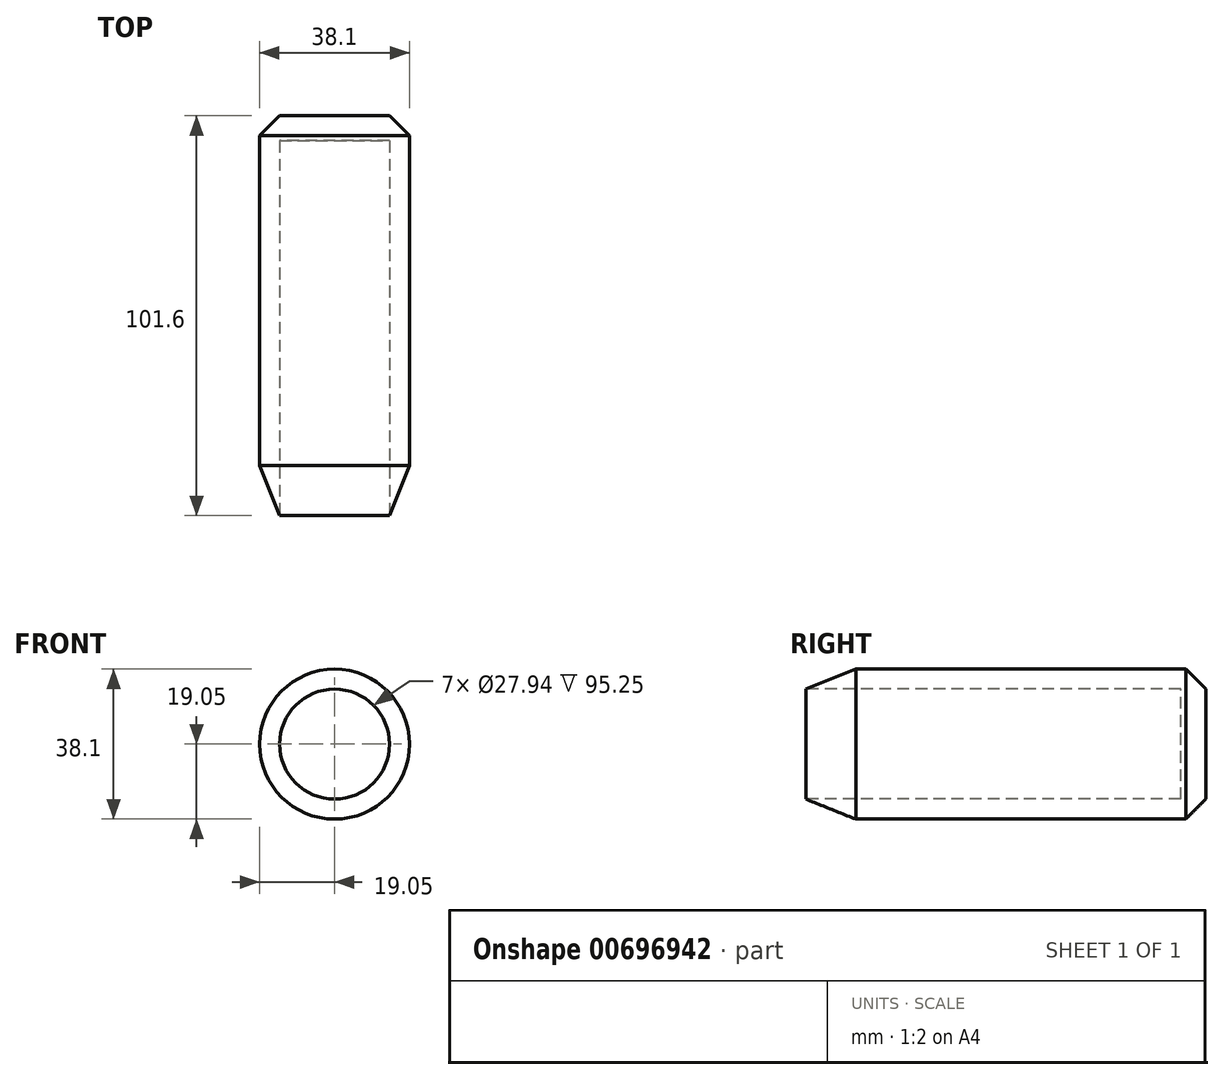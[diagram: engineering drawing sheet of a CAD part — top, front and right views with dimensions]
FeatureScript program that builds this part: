
annotation { "Feature Type Name" : "Feature", "Feature Type Description" : "" }
export const myFeature = defineFeature(function(context is Context, id is Id, definition is map)
    precondition{}
    {
        {
            var Q0;
            Q0=qCreatedBy(makeId("Front.planeOp"),FACE);
            var sketch = newSketch(context, id + "F0", { "sketchPlane" : qUnion([Q0])});
            skCircle(sketch, "E0", {"center": v(0, 0) * mm, "radius": 12.7 * mm});
            skCircle(sketch, "E1", {"center": v(0, 0) * mm, "radius": 19.05 * mm});
            skSolve(sketch);
        }
        {
            var Q0;
            Q0=makeQuery(id+"F0.imprint","IMPRINT",FACE,{"disambiguationData":[TD([[makeQuery(id+"F0.imprint","IMPRINT",EDGE,{"derivedFrom":sQuery(id+"F0.wireOp",EDGE,"E0")}),-1.0]])]});
            var Q1;
            Q1=makeQuery(id+"F0.imprint","IMPRINT",FACE,{"disambiguationData":[TD([[makeQuery(id+"F0.imprint","IMPRINT",EDGE,{"derivedFrom":sQuery(id+"F0.wireOp",EDGE,"E0")}),1.0]])]});
            extrude(context, id + "F1", {"entities" : qUnion([Q0, Q1]), "depth" : 101.6 * mm, "offsetDistance" : 25.4 * mm});
        }
        {
            var Q0;
            Q0=makeQuery(id+"F1.opExtrude","CAP_EDGE",EDGE,{"disambiguationData":[OSD([sQuery(id+"F0.wireOp",EDGE,"E1")])],"isStart":false});
            chamfer(context, id + "F2", {"entities" : qUnion([Q0]), "chamferType" : ChamferType.TWO_OFFSETS, "width1" : 5.08 * mm, "oppositeDirection" : false, "width2" : 12.7 * mm, "tangentPropagation" : true});
        }
        {
            var Q0;
            Q0=makeQuery(id+"F1.opExtrude","CAP_FACE",FACE,{"disambiguationData":[OSD([sQuery(id+"F0.wireOp",EDGE,"E1")])],"isStart":false});
            extrude(context, id + "F3", {"entities" : qUnion([Q0]), "operationType" : NewBodyOperationType.REMOVE, "oppositeDirection" : true, "depth" : 95.25 * mm, "offsetDistance" : 25.4 * mm});
        }
        {
            var Q0;
            Q0=makeQuery(id+"F1.opExtrude","CAP_EDGE",EDGE,{"disambiguationData":[OSD([sQuery(id+"F0.wireOp",EDGE,"E1")])],"isStart":true});
            chamfer(context, id + "F4", {"entities" : qUnion([Q0]), "width" : 5.08 * mm, "tangentPropagation" : true});
        }
    });
